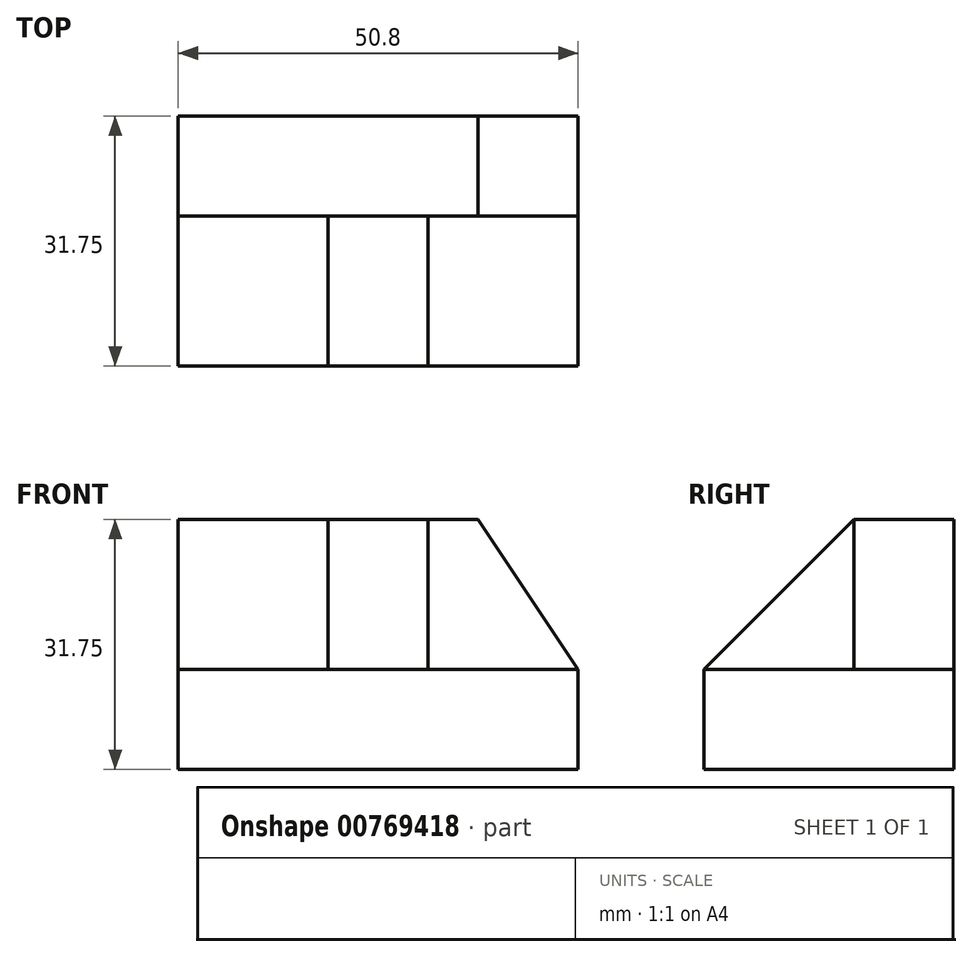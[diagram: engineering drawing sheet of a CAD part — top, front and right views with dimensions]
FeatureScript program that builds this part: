
annotation { "Feature Type Name" : "Feature", "Feature Type Description" : "" }
export const myFeature = defineFeature(function(context is Context, id is Id, definition is map)
    precondition{}
    {
        {
            var Q0;
            Q0=qCreatedBy(makeId("Front.planeOp"),FACE);
            var sketch = newSketch(context, id + "F0", { "sketchPlane" : qUnion([Q0])});
            skLineSegment(sketch, "E0", {"start": v(0, 0) * mm, "end": v(50.8, 0) * mm});
            skLineSegment(sketch, "E1", {"start": v(50.8, 0) * mm, "end": v(50.8, 31.75) * mm});
            skLineSegment(sketch, "E2", {"start": v(50.8, 31.75) * mm, "end": v(0, 31.75) * mm});
            skLineSegment(sketch, "E3", {"start": v(0, 31.75) * mm, "end": v(0, 0) * mm});
            skSolve(sketch);
        }
        {
            var Q0;
            Q0=makeQuery(id+"F0.imprint","IMPRINT",FACE,{"disambiguationData":[TD([[makeQuery(id+"F0.imprint","IMPRINT",EDGE,{"derivedFrom":sQuery(id+"F0.wireOp",EDGE,"E0")}),1.0]])]});
            extrude(context, id + "F1", {"entities" : qUnion([Q0]), "depth" : 31.75 * mm, "offsetDistance" : 25.4 * mm});
        }
        {
            var Q0;
            Q0=makeQuery(id+"F1.opExtrude","SWEPT_FACE",FACE,{"disambiguationData":[OSD([sQuery(id+"F0.wireOp",EDGE,"E2")])]});
            var sketch = newSketch(context, id + "F2", { "sketchPlane" : qUnion([Q0])});
            skLineSegment(sketch, "E4", {"start": v(0, 0) * mm, "end": v(0, -12.7) * mm});
            skLineSegment(sketch, "E5", {"start": v(0, -12.7) * mm, "end": v(50.8, -12.7) * mm});
            skSolve(sketch);
        }
        {
            var Q0;
            Q0 = qSketchRegion(id + "F2", true);
            var Q1;
            {var subQ0=sQuery(id+"F2.wireOp",EDGE,"E5");Q1=makeQuery(id+"F2.imprint","IMPRINT",FACE,{"disambiguationData":[TD([[makeQuery(id+"F2.imprint","IMPRINT",EDGE,{"derivedFrom":subQ0}),-1.0]])]});}
            extrude(context, id + "F3", {"entities" : qUnion([Q0, Q1]), "operationType" : NewBodyOperationType.REMOVE, "oppositeDirection" : true, "depth" : 19.05 * mm, "offsetDistance" : 25.4 * mm});
        }
        {
            var Q0;
            Q0=makeQuery(id+"F3.boolean.opBoolean","COPY",FACE,{"derivedFrom":makeQuery(id+"F3.opExtrude","SWEPT_FACE",FACE,{"disambiguationData":[OSD([sQuery(id+"F2.wireOp",EDGE,"E5")])]})});
            var sketch = newSketch(context, id + "F4", { "sketchPlane" : qUnion([Q0])});
            skLineSegment(sketch, "E6", {"start": v(0, 31.75) * mm, "end": v(38.1, 31.75) * mm});
            skLineSegment(sketch, "E7", {"start": v(38.1, 31.75) * mm, "end": v(50.8, 12.7) * mm});
            skSolve(sketch);
        }
        {
            var Q0;
            Q0 = qSketchRegion(id + "F4", true);
            var Q1;
            {var subQ0=sQuery(id+"F4.wireOp",EDGE,"E7");Q1=makeQuery(id+"F4.imprint","IMPRINT",FACE,{"disambiguationData":[TD([[makeQuery(id+"F4.imprint","IMPRINT",EDGE,{"derivedFrom":subQ0}),1.0]])]});}
            extrude(context, id + "F5", {"entities" : qUnion([Q0, Q1]), "operationType" : NewBodyOperationType.REMOVE, "endBound" : BoundingType.THROUGH_ALL, "oppositeDirection" : true, "depth" : 25.4 * mm, "offsetDistance" : 25.4 * mm});
        }
        {
            var Q0;
            Q0=makeQuery(id+"F3.boolean.opBoolean","COPY",FACE,{"derivedFrom":makeQuery(id+"F3.opExtrude","SWEPT_FACE",FACE,{"disambiguationData":[OSD([sQuery(id+"F2.wireOp",EDGE,"E5")])]})});
            var sketch = newSketch(context, id + "F6", { "sketchPlane" : qUnion([Q0])});
            skLineSegment(sketch, "E8", {"start": v(0, 31.75) * mm, "end": v(19.05, 31.75) * mm});
            skLineSegment(sketch, "E9", {"start": v(19.05, 31.75) * mm, "end": v(19.05, 12.7) * mm});
            skLineSegment(sketch, "E10", {"start": v(19.05, 12.7) * mm, "end": v(31.75, 12.7) * mm});
            skLineSegment(sketch, "E11", {"start": v(31.75, 12.7) * mm, "end": v(31.75, 31.75) * mm});
            skSolve(sketch);
        }
        {
            var Q0;
            {var subQ0=sQuery(id+"F6.wireOp",EDGE,"E9");Q0=makeQuery(id+"F6.imprint","IMPRINT",FACE,{"disambiguationData":[TD([[makeQuery(id+"F6.imprint","IMPRINT",EDGE,{"derivedFrom":subQ0}),1.0]])]});}
            extrude(context, id + "F7", {"entities" : qUnion([Q0]), "operationType" : NewBodyOperationType.ADD, "depth" : 19.05 * mm, "offsetDistance" : 25.4 * mm});
        }
        {
            var Q0;
            Q0=makeQuery(id+"F7.opExtrude","SWEPT_FACE",FACE,{"disambiguationData":[OSD([sQuery(id+"F6.wireOp",EDGE,"E11")])]});
            var sketch = newSketch(context, id + "F8", { "sketchPlane" : qUnion([Q0])});
            skLineSegment(sketch, "E12", {"start": v(-12.7, 31.75) * mm, "end": v(-31.75, 12.7) * mm});
            skSolve(sketch);
        }
        {
            var Q0;
            Q0 = qSketchRegion(id + "F8", true);
            var Q1;
            Q1=makeQuery(id+"F8.imprint","IMPRINT",FACE,{"disambiguationData":[TD([[makeQuery(id+"F8.imprint","IMPRINT",EDGE,{"derivedFrom":sQuery(id+"F8.wireOp",EDGE,"E12")}),-1.0]])]});
            extrude(context, id + "F9", {"entities" : qUnion([Q0, Q1]), "operationType" : NewBodyOperationType.REMOVE, "endBound" : BoundingType.THROUGH_ALL, "oppositeDirection" : true, "depth" : 25.4 * mm, "offsetDistance" : 25.4 * mm});
        }
    });
